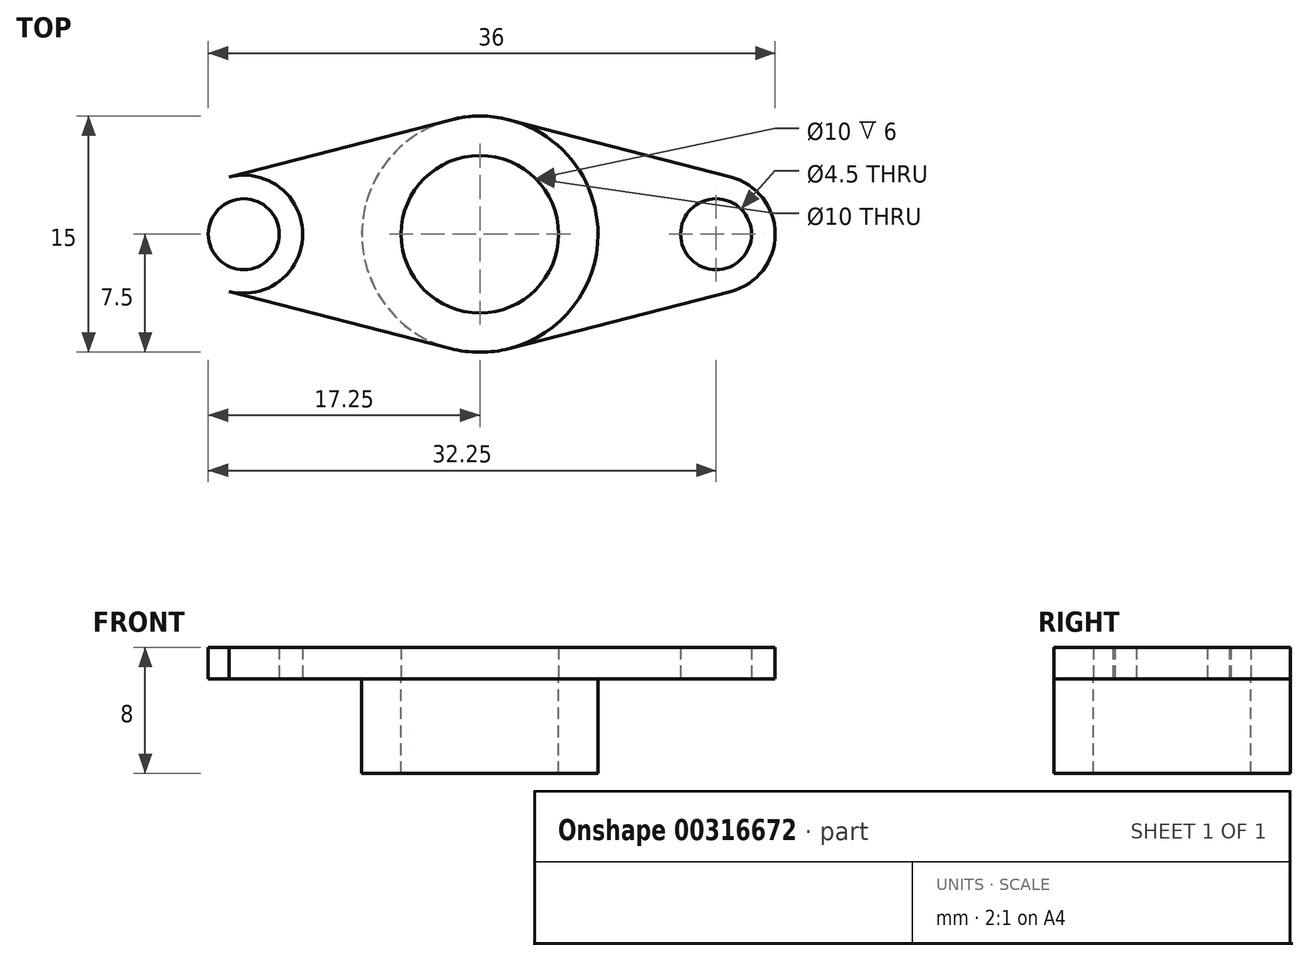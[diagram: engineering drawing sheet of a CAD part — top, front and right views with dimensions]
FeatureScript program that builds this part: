
annotation { "Feature Type Name" : "Feature", "Feature Type Description" : "" }
export const myFeature = defineFeature(function(context is Context, id is Id, definition is map)
    precondition{}
    {
        {
            var Q0;
            Q0=qCreatedBy(makeId("Top.planeOp"),FACE);
            var sketch = newSketch(context, id + "F0", { "sketchPlane" : qUnion([Q0])});
            skCircle(sketch, "E0", {"center": v(0, 0) * mm, "radius": 7.5 * mm});
            skCircle(sketch, "E1", {"center": v(0, 0) * mm, "radius": 5 * mm});
            skCircle(sketch, "E2", {"center": v(15, 0) * mm, "radius": 2.25 * mm});
            skCircle(sketch, "E3", {"center": v(15, 0) * mm, "radius": 3.75 * mm});
            skLineSegment(sketch, "E4", {"start": v(1.88, 7.26) * mm, "end": v(15.94, 3.63) * mm});
            skLineSegment(sketch, "E5", {"start": v(1.87, -7.26) * mm, "end": v(15.94, -3.63) * mm});
            skCircle(sketch, "E6.MirrorC", {"center": v(-15, 0) * mm, "radius": 2.25 * mm});
            skLineSegment(sketch, "E7.MirrorCS", {"start": v(-1.88, 7.26) * mm, "end": v(-15.94, 3.63) * mm});
            skCircle(sketch, "E8.MirrorC", {"center": v(-15, 0) * mm, "radius": 3.75 * mm});
            skLineSegment(sketch, "E9.MirrorCS", {"start": v(-1.87, -7.26) * mm, "end": v(-15.94, -3.63) * mm});
            skSolve(sketch);
        }
        {
            var Q0;
            Q0=makeQuery(id+"F0.imprint","IMPRINT",FACE,{"disambiguationData":[TD([[makeQuery(id+"F0.imprint","IMPRINT",EDGE,{"derivedFrom":sQuery(id+"F0.wireOp",EDGE,"E6.MirrorC")}),1.0]])]});
            var Q1;
            {var subQ0=sQuery(id+"F0.wireOp",EDGE,"E7.MirrorCS");Q1=makeQuery(id+"F0.imprint","IMPRINT",FACE,{"disambiguationData":[TD([[makeQuery(id+"F0.imprint","IMPRINT",EDGE,{"derivedFrom":subQ0}),1.0]])]});}
            var Q2;
            {var subQ0=sQuery(id+"F0.wireOp",EDGE,"E4");Q2=makeQuery(id+"F0.imprint","IMPRINT",FACE,{"disambiguationData":[TD([[makeQuery(id+"F0.imprint","IMPRINT",EDGE,{"derivedFrom":subQ0}),-1.0]])]});}
            var Q3;
            Q3=makeQuery(id+"F0.imprint","IMPRINT",FACE,{"disambiguationData":[TD([[makeQuery(id+"F0.imprint","IMPRINT",EDGE,{"derivedFrom":sQuery(id+"F0.wireOp",EDGE,"E2")}),-1.0]])]});
            var Q4;
            Q4=makeQuery(id+"F0.imprint","IMPRINT",FACE,{"disambiguationData":[TD([[makeQuery(id+"F0.imprint","IMPRINT",EDGE,{"derivedFrom":sQuery(id+"F0.wireOp",EDGE,"E1")}),-1.0]])]});
            extrude(context, id + "F1", {"entities" : qUnion([Q0, Q1, Q2, Q3, Q4]), "depth" : 2 * mm});
        }
        {
            var Q0;
            Q0=makeQuery(id+"F0.imprint","IMPRINT",FACE,{"disambiguationData":[TD([[makeQuery(id+"F0.imprint","IMPRINT",EDGE,{"derivedFrom":sQuery(id+"F0.wireOp",EDGE,"E1")}),-1.0]])]});
            extrude(context, id + "F2", {"entities" : qUnion([Q0]), "oppositeDirection" : true, "depth" : 6 * mm});
        }
    });
